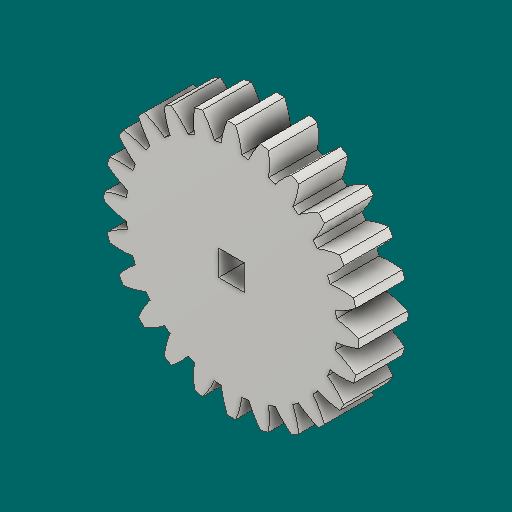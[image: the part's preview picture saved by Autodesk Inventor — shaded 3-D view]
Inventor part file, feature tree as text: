
AUTODESK INVENTOR PART (.ipt)
format: ipt  version: 2023.1 (Build 271208000, 208)  size: 278,528 bytes
history: native  units: in
note: dims shown in document units (in); Inventor stores cm internally (conversion verified against a paired STEP export)
features: other x12, sketch x3, plane x3
ambient origin geometry x8: Origin, YZ Plane, XZ Plane, XY Plane, X Axis, Y Axis, Z Axis, Center Point
bodies: Solid1 (feature_tree)
feature tree (18):
  other  "Spur Gear1"
  other  "Solid1::Spur Gear1"
  other  "TaggingFeature1"
  sketch  "Sketch1"  dims[d0=0.3937in]
  sketch  "Sketch2"  dims[d9=0.0in]
  sketch  "Sketch3"  dims[d14=0.0in d15=1.2in d16=0.0in d17=0.0in d18=0.0in d19=1.2in]
  plane  "XZ Plane_1"
  plane  "Work Plane2"
  plane  "Work Plane3"
  other  "Srf1"
  other  "Srf1::Derived"
  other  "Start plane iMate"
  other  "Distance iMate"
  other  "Position iMate"
  other  "Mesh iMate"
  other  "Axis iMate"
  other  "Mesh iMate2"
  other  "Align iMate"
